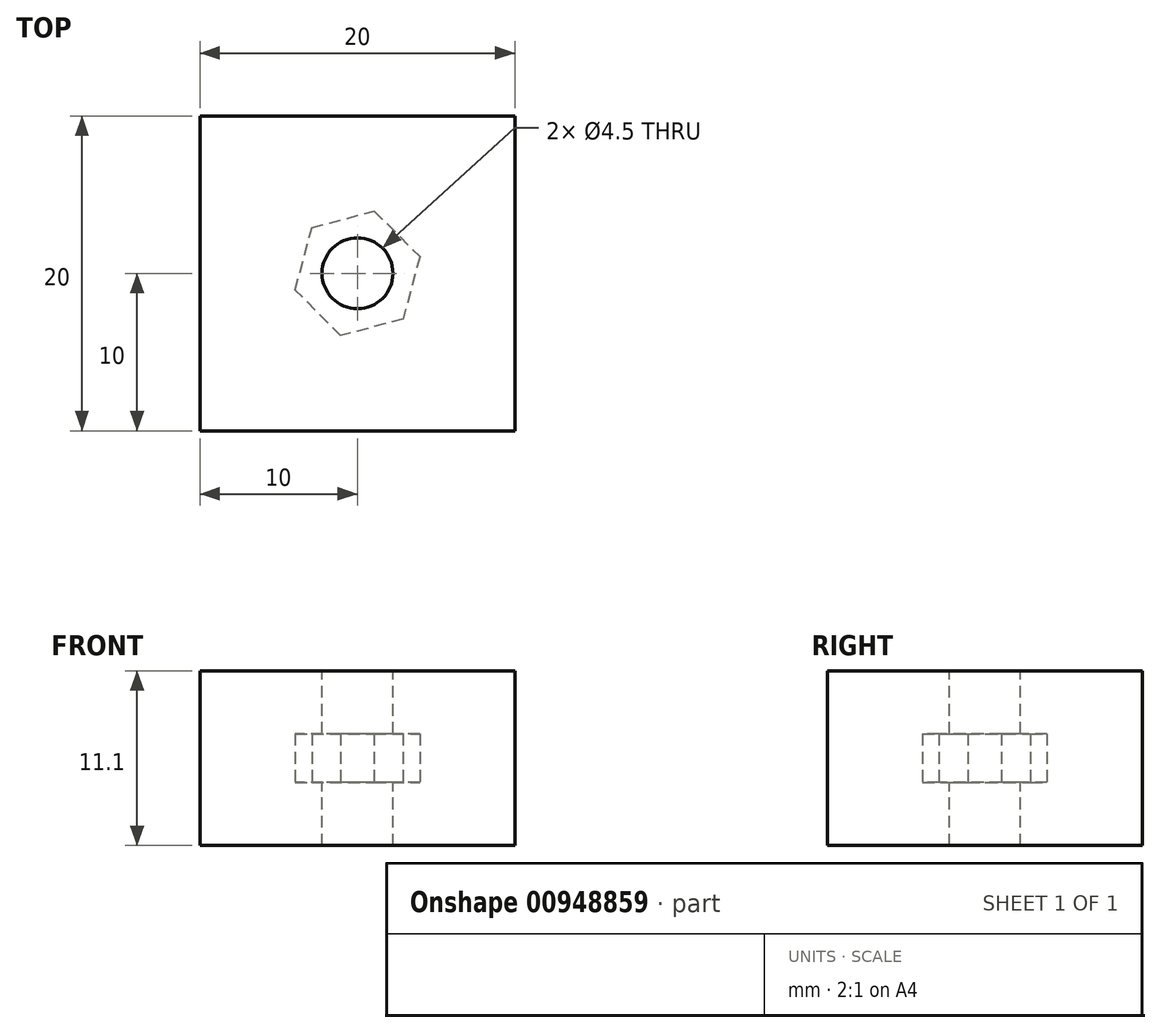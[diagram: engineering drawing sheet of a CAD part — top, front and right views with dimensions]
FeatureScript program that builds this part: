
annotation { "Feature Type Name" : "Feature", "Feature Type Description" : "" }
export const myFeature = defineFeature(function(context is Context, id is Id, definition is map)
    precondition{}
    {
        {
            var Q0;
            Q0=qCreatedBy(makeId("Top.planeOp"),FACE);
            var sketch = newSketch(context, id + "F0", { "sketchPlane" : qUnion([Q0])});
            skLineSegment(sketch, "E0.bottom", {"start": v(0, 0) * mm, "end": v(20, 0) * mm});
            skLineSegment(sketch, "E0.top", {"start": v(0, -20) * mm, "end": v(20, -20) * mm});
            skLineSegment(sketch, "E0.left", {"start": v(0, 0) * mm, "end": v(0, -20) * mm});
            skLineSegment(sketch, "E0.right", {"start": v(20, 0) * mm, "end": v(20, -20) * mm});
            skSolve(sketch);
        }
        {
            var Q0;
            Q0=makeQuery(id+"F0.imprint","IMPRINT",FACE,{"disambiguationData":[TD([[makeQuery(id+"F0.imprint","IMPRINT",EDGE,{"derivedFrom":sQuery(id+"F0.wireOp",EDGE,"E0.bottom")}),-1.0]])]});
            extrude(context, id + "F1", {"entities" : qUnion([Q0]), "depth" : 4 * mm, "offsetDistance" : 25 * mm});
        }
        {
            var Q0;
            Q0=makeQuery(id+"F1.opExtrude","CAP_FACE",FACE,{"disambiguationData":[OSD([sQuery(id+"F0.wireOp",EDGE,"E0.bottom"),sQuery(id+"F0.wireOp",EDGE,"E0.top"),sQuery(id+"F0.wireOp",EDGE,"E0.left"),sQuery(id+"F0.wireOp",EDGE,"E0.right")])],"isStart":false});
            var sketch = newSketch(context, id + "F2", { "sketchPlane" : qUnion([Q0])});
            skLineSegment(sketch, "E1", {"start": v(0, -20) * mm, "end": v(20, 0) * mm});
            skLineSegment(sketch, "E2", {"start": v(0, 0) * mm, "end": v(20, -20) * mm});
            skCircle(sketch, "E3.cCircle", {"center": v(10, -10) * mm, "radius": 3.55 * mm, "construction": true});
            skLineSegment(sketch, "E3.0", {"start": v(11.06, -6.04) * mm, "end": v(13.96, -8.94) * mm});
            skLineSegment(sketch, "E3.1", {"start": v(13.96, -8.94) * mm, "end": v(12.9, -12.9) * mm});
            skLineSegment(sketch, "E3.2", {"start": v(12.9, -12.9) * mm, "end": v(8.94, -13.96) * mm});
            skLineSegment(sketch, "E3.3", {"start": v(8.94, -13.96) * mm, "end": v(6.04, -11.06) * mm});
            skLineSegment(sketch, "E3.4", {"start": v(6.04, -11.06) * mm, "end": v(7.1, -7.1) * mm});
            skLineSegment(sketch, "E3.5", {"start": v(7.1, -7.1) * mm, "end": v(11.06, -6.04) * mm});
            skPoint(sketch, "E3.0.midPoint", {"position": v(12.51, -7.49) * mm});
            skSolve(sketch);
        }
        {
            var Q0;
            {var subQ0=sQuery(id+"F2.wireOp",EDGE,"E3.5");Q0=makeQuery(id+"F2.imprint","IMPRINT",FACE,{"disambiguationData":[TD([[makeQuery(id+"F2.imprint","IMPRINT",EDGE,{"derivedFrom":subQ0}),1.0]])]});}
            var Q1;
            {var subQ0=sQuery(id+"F2.wireOp",EDGE,"E3.1");Q1=makeQuery(id+"F2.imprint","IMPRINT",FACE,{"disambiguationData":[TD([[makeQuery(id+"F2.imprint","IMPRINT",EDGE,{"derivedFrom":subQ0}),1.0]])]});}
            var Q2;
            {var subQ0=sQuery(id+"F2.wireOp",EDGE,"E3.4");Q2=makeQuery(id+"F2.imprint","IMPRINT",FACE,{"disambiguationData":[TD([[makeQuery(id+"F2.imprint","IMPRINT",EDGE,{"derivedFrom":subQ0}),1.0]])]});}
            var Q3;
            {var subQ0=sQuery(id+"F2.wireOp",EDGE,"E3.2");Q3=makeQuery(id+"F2.imprint","IMPRINT",FACE,{"disambiguationData":[TD([[makeQuery(id+"F2.imprint","IMPRINT",EDGE,{"derivedFrom":subQ0}),1.0]])]});}
            extrude(context, id + "F3", {"entities" : qUnion([Q0, Q1, Q2, Q3]), "operationType" : NewBodyOperationType.ADD, "depth" : 3.1 * mm, "offsetDistance" : 25 * mm});
        }
        {
            var Q0;
            Q0=makeQuery(id+"F3.opExtrude","CAP_FACE",FACE,{"disambiguationData":[OSD([sQuery(id+"F0.wireOp",EDGE,"E0.bottom"),sQuery(id+"F0.wireOp",EDGE,"E0.top"),sQuery(id+"F0.wireOp",EDGE,"E0.left"),sQuery(id+"F0.wireOp",EDGE,"E0.right"),sQuery(id+"F2.wireOp",EDGE,"E3.0"),sQuery(id+"F2.wireOp",EDGE,"E3.1"),sQuery(id+"F2.wireOp",EDGE,"E3.2"),sQuery(id+"F2.wireOp",EDGE,"E3.3"),sQuery(id+"F2.wireOp",EDGE,"E3.4"),sQuery(id+"F2.wireOp",EDGE,"E3.5")])],"isStart":false});
            var sketch = newSketch(context, id + "F4", { "sketchPlane" : qUnion([Q0])});
            skLineSegment(sketch, "E4.bottom", {"start": v(0, 0) * mm, "end": v(20, 0) * mm});
            skLineSegment(sketch, "E4.top", {"start": v(0, -20) * mm, "end": v(20, -20) * mm});
            skLineSegment(sketch, "E4.left", {"start": v(0, 0) * mm, "end": v(0, -20) * mm});
            skLineSegment(sketch, "E4.right", {"start": v(20, 0) * mm, "end": v(20, -20) * mm});
            skSolve(sketch);
        }
        {
            var Q0;
            Q0=makeQuery(id+"F4.imprint","IMPRINT",FACE,{"disambiguationData":[TD([[makeQuery(id+"F4.imprint","IMPRINT",EDGE,{"derivedFrom":makeQuery(id+"F3.opExtrude","CAP_EDGE",EDGE,{"disambiguationData":[OSD([sQuery(id+"F2.wireOp",EDGE,"E3.0")])],"isStart":false})}),-1.0]])]});
            var Q1;
            Q1=makeQuery(id+"F4.imprint","IMPRINT",FACE,{"disambiguationData":[TD([[makeQuery(id+"F4.imprint","IMPRINT",EDGE,{"derivedFrom":sQuery(id+"F4.wireOp",EDGE,"E4.bottom")}),-1.0]])]});
            extrude(context, id + "F5", {"entities" : qUnion([Q0, Q1]), "operationType" : NewBodyOperationType.ADD, "depth" : 4 * mm, "offsetDistance" : 25 * mm});
        }
        {
            var Q0;
            Q0=makeQuery(id+"F5.opExtrude","CAP_FACE",FACE,{"disambiguationData":[OSD([sQuery(id+"F4.wireOp",EDGE,"E4.bottom"),sQuery(id+"F4.wireOp",EDGE,"E4.top"),sQuery(id+"F4.wireOp",EDGE,"E4.left"),sQuery(id+"F4.wireOp",EDGE,"E4.right")])],"isStart":false});
            var sketch = newSketch(context, id + "F6", { "sketchPlane" : qUnion([Q0])});
            skCircle(sketch, "E5", {"center": v(10, -10) * mm, "radius": 2.25 * mm});
            skPoint(sketch, "E6.start.orphan", {"position": v(0, 0) * mm});
            skPoint(sketch, "E7.start.orphan", {"position": v(20, -20) * mm});
            skSolve(sketch);
        }
        {
            var Q0;
            Q0=makeQuery(id+"F6.imprint","IMPRINT",FACE,{"disambiguationData":[TD([[makeQuery(id+"F6.imprint","IMPRINT",EDGE,{"derivedFrom":sQuery(id+"F6.wireOp",EDGE,"E5")}),1.0]])]});
            extrude(context, id + "F7", {"entities" : qUnion([Q0]), "operationType" : NewBodyOperationType.REMOVE, "oppositeDirection" : true, "depth" : 25 * mm, "offsetDistance" : 25 * mm});
        }
    });
